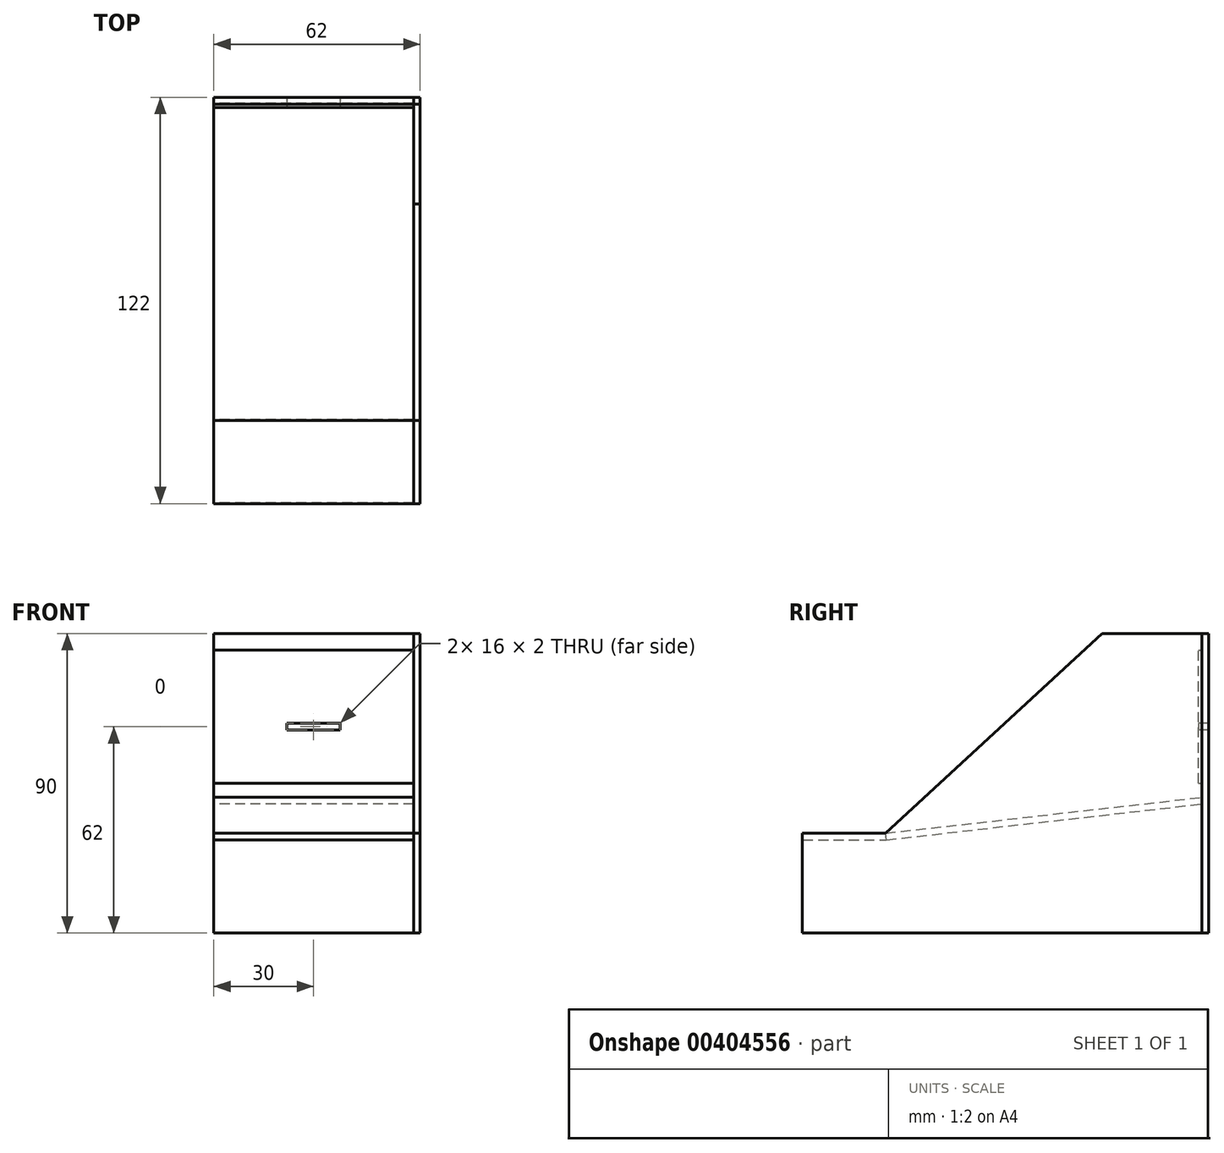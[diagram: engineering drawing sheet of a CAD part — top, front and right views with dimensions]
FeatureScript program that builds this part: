
annotation { "Feature Type Name" : "Feature", "Feature Type Description" : "" }
export const myFeature = defineFeature(function(context is Context, id is Id, definition is map)
    precondition{}
    {
        {
            var Q0;
            Q0=qCreatedBy(makeId("Top.planeOp"),FACE);
            var sketch = newSketch(context, id + "F0", { "sketchPlane" : qUnion([Q0])});
            skLineSegment(sketch, "E0.bottom", {"start": v(0, 0) * mm, "end": v(60, 0) * mm});
            skLineSegment(sketch, "E0.top", {"start": v(0, 120) * mm, "end": v(60, 120) * mm});
            skLineSegment(sketch, "E0.left", {"start": v(0, 0) * mm, "end": v(0, 120) * mm});
            skLineSegment(sketch, "E0.right", {"start": v(60, 0) * mm, "end": v(60, 120) * mm});
            skSolve(sketch);
        }
        {
            var Q0;
            Q0 = qSketchRegion(id + "F0", true);
            var Q1;
            Q1=sQuery(id+"F0.wireOp",EDGE,"E0.left");
            var Q2;
            Q2=sQuery(id+"F0.wireOp",EDGE,"E0.right");
            var Q3;
            Q3=sQuery(id+"F0.wireOp",EDGE,"E0.top");
            extrude(context, id + "F1", {"entities" : qUnion([Q0]), "bodyType" : ToolBodyType.SURFACE, "surfaceEntities" : qUnion([Q1, Q2, Q3]), "depth" : 90 * mm});
        }
        {
            var Q0;
            Q0=makeQuery(id+"F1.opExtrude","SWEPT_FACE",FACE,{"disambiguationData":[OSD([sQuery(id+"F0.wireOp",EDGE,"E0.right")])]});
            var sketch = newSketch(context, id + "F2", { "sketchPlane" : qUnion([Q0])});
            skLineSegment(sketch, "E1", {"start": v(-120, 90) * mm, "end": v(-90, 90) * mm});
            skLineSegment(sketch, "E2", {"start": v(0, 0) * mm, "end": v(0, 30) * mm});
            skLineSegment(sketch, "E3", {"start": v(0, 30) * mm, "end": v(-25, 30) * mm});
            skLineSegment(sketch, "E4", {"start": v(-25, 30) * mm, "end": v(-90, 90) * mm});
            skLineSegment(sketch, "E5", {"start": v(-25, 30) * mm, "end": v(-120, 40.8) * mm});
            skSolve(sketch);
        }
        {
            var Q0;
            Q0=sQuery(id+"F2.wireOp",EDGE,"E5");
            extrude(context, id + "F3", {"bodyType" : ToolBodyType.SURFACE, "surfaceEntities" : qUnion([Q0]), "depth" : 60 * mm});
        }
        {
            var Q0;
            Q0=makeQuery(id+"F2.imprint","IMPRINT",FACE,{"disambiguationData":[TD([[makeQuery(id+"F2.imprint","IMPRINT",EDGE,{"derivedFrom":sQuery(id+"F2.wireOp",EDGE,"E2")}),1.0]])]});
            var Q1;
            {var subQ0=sQuery(id+"F2.wireOp",EDGE,"E1");Q1=makeQuery(id+"F2.imprint","IMPRINT",FACE,{"disambiguationData":[TD([[makeQuery(id+"F2.imprint","IMPRINT",EDGE,{"derivedFrom":subQ0}),-1.0]])]});}
            extrude(context, id + "F4", {"entities" : qUnion([Q0, Q1]), "oppositeDirection" : true, "depth" : 2 * mm});
        }
        {
            var Q0;
            Q0=sQuery(id+"F2.wireOp",EDGE,"E3");
            extrude(context, id + "F5", {"bodyType" : ToolBodyType.SURFACE, "surfaceEntities" : qUnion([Q0]), "depth" : 60 * mm});
        }
        {
            var Q0;
            Q0=makeQuery(id+"F1.opExtrude","SWEPT_FACE",FACE,{"disambiguationData":[OSD([sQuery(id+"F0.wireOp",EDGE,"E0.top")])]});
            var Q1;
            Q1=makeQuery(id+"F4.opExtrude","SWEPT_FACE",FACE,{"disambiguationData":[OSD([sQuery(id+"F0.wireOp",VERTEX,"E0.top.end")])]});
            var Q2;
            Q2=makeQuery(id+"FEGVrS68jlSHVTY_4.opExtrude","SWEPT_FACE",FACE,{"disambiguationData":[OSD([sQuery(id+"F0.wireOp",VERTEX,"E0.top.start")])]});
            extrude(context, id + "F6", {"entities" : qUnion([Q0, Q1, Q2]), "oppositeDirection" : true, "depth" : 2 * mm});
        }
        {
            var Q0;
            Q0=makeQuery(id+"F3.opExtrude","SWEPT_FACE",FACE,{"disambiguationData":[OSD([sQuery(id+"F2.wireOp",EDGE,"E5")])]});
            var Q1;
            Q1=makeQuery(id+"F5.opExtrude","SWEPT_FACE",FACE,{"disambiguationData":[OSD([sQuery(id+"F2.wireOp",EDGE,"E3")])]});
            extrude(context, id + "F7", {"entities" : qUnion([Q0, Q1]), "oppositeDirection" : true, "depth" : 2 * mm});
        }
        {
            var Q0;
            Q0=makeQuery(id+"F1.opExtrude","SWEPT_FACE",FACE,{"disambiguationData":[OSD([sQuery(id+"F0.wireOp",EDGE,"E0.top")])]});
            var sketch = newSketch(context, id + "F8", { "sketchPlane" : qUnion([Q0])});
            skLineSegment(sketch, "E6", {"start": v(0, 90) * mm, "end": v(0, 85) * mm, "construction": true});
            skLineSegment(sketch, "E7.bottom", {"start": v(0, 85) * mm, "end": v(60, 85) * mm});
            skLineSegment(sketch, "E7.top", {"start": v(0, 45) * mm, "end": v(60, 45) * mm});
            skLineSegment(sketch, "E7.left", {"start": v(0, 85) * mm, "end": v(0, 45) * mm});
            skLineSegment(sketch, "E7.right", {"start": v(60, 85) * mm, "end": v(60, 45) * mm});
            skSolve(sketch);
        }
        {
            var Q0;
            Q0 = qSketchRegion(id + "F8", true);
            extrude(context, id + "F9", {"entities" : qUnion([Q0]), "depth" : 1 * mm});
        }
        {
            var Q0;
            Q0=makeQuery(id+"F9.opExtrude","CAP_FACE",FACE,{"disambiguationData":[OSD([sQuery(id+"F8.wireOp",EDGE,"E7.bottom"),sQuery(id+"F8.wireOp",EDGE,"E7.top"),sQuery(id+"F8.wireOp",EDGE,"E7.left"),sQuery(id+"F8.wireOp",EDGE,"E7.right")])],"isStart":false});
            var sketch = newSketch(context, id + "F10", { "sketchPlane" : qUnion([Q0])});
            skLineSegment(sketch, "E8", {"start": v(0, 45) * mm, "end": v(30, 45) * mm, "construction": true});
            skLineSegment(sketch, "E9", {"start": v(30, 45) * mm, "end": v(30, 61) * mm, "construction": true});
            skLineSegment(sketch, "E10", {"start": v(30, 61) * mm, "end": v(38, 61) * mm});
            skLineSegment(sketch, "E11", {"start": v(38, 61) * mm, "end": v(38, 63) * mm});
            skLineSegment(sketch, "E12", {"start": v(38, 63) * mm, "end": v(22, 63) * mm});
            skLineSegment(sketch, "E13", {"start": v(22, 63) * mm, "end": v(22, 61) * mm});
            skLineSegment(sketch, "E14", {"start": v(22, 61) * mm, "end": v(30, 61) * mm});
            skSolve(sketch);
        }
        {
            var Q0;
            Q0 = qSketchRegion(id + "F10", true);
            extrude(context, id + "F11", {"entities" : qUnion([Q0]), "operationType" : NewBodyOperationType.REMOVE, "oppositeDirection" : true, "depth" : 3 * mm});
        }
    });
